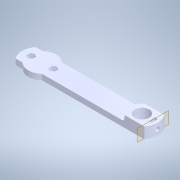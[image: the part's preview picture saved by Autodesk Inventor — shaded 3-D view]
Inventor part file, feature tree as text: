
AUTODESK INVENTOR PART (.ipt)
format: ipt  version: 2021 (Build 250183000, 183)  size: 411,648 bytes
history: native  units: in
note: dims shown in document units (in); Inventor stores cm internally (conversion verified against a paired STEP export)
features: sketch x20, extrude x17, fillet x3, projected_geometry x2, delete_face x1, chamfer x1, hole x1, plane x1, other x1
ambient origin geometry x8: Origin, YZ Plane, XZ Plane, XY Plane, X Axis, Y Axis, Z Axis, Center Point
bodies: Solid1 (feature_tree)
feature tree (47):
  extrude  "Extrusion1"  Depth=0.3937in TaperAngle=0.0deg
  extrude  "Extrusion2"  TaperAngle=0.0deg  [1 undecoded]
  sketch  "Sketch5"  dims[d9=0.3937in d10=0.0in d11=0.878in d12=0.3937in d13=0.0in]
  delete_face  "Delete Face1"
  extrude  "Extrusion4"  Depth=0.9843in
  extrude  "Extrusion5"  Depth=0.878in
  chamfer  "Chamfer1"  Distance=0.3937in
  sketch  "Sketch8"  dims[d32=0.3937in d33=0.0in d34=0.0787in d35=0.0787in d36=0.0in]
  extrude  "Extrusion7"  Depth=0.0787in
  extrude  "Extrusion9"  Depth=3.5433in
  extrude  "Extrusion8"  Depth=0.0787in
  fillet  "Fillet2"  Radius=0.0787in
  hole  "Hole1"  [1 undecoded]
  extrude  "Extrusion10"  Depth=0.0787in
  extrude  "Extrusion11"  Depth=0.0787in
  extrude  "Extrusion12"  Depth=0.1378in
  fillet  "Fillet3"  Radius=0.3937in
  extrude  "Extrusion3"  Depth=0.0118in
  extrude  "Extrusion13"  Depth=0.0394in
  extrude  "Extrusion14"  TaperAngle=0.0deg  [1 undecoded]
  extrude  "Extrusion15"  Depth=0.5906in
  extrude  "Extrusion16"  Depth=0.3937in TaperAngle=0.0deg
  plane  "Work Plane1"
  extrude  "Extrusion17"  Depth=0.3937in TaperAngle=0.0deg
  extrude  "Extrusion18"  Depth=0.3937in
  fillet  "Fillet4"  Radius=0.1969in
  sketch  "Sketch1"  dims[d0=0.7874in d1=0.3937in d2=0.0in]
  sketch  "Sketch2"  dims[d3=0.3937in d4=0.0in d5=0.0in]
  sketch  "Sketch4"  dims[d6=0.3937in d7=0.0in d8=0.9843in]
  sketch  "Sketch6"  dims[d14=0.0197in d15=0.0787in d16=45.0deg d28=0.7087in]
  sketch  "Sketch7"  dims[d29=0.3937in d30=0.0in d31=3.5433in]
  sketch  "Sketch11"  dims[d37=0.7874in d39=0.4921in]
  sketch  "Sketch12"  dims[d40=0.1378in d41=0.2362in d42=0.1575in d43=0.0787in d44=90.0deg d45=0.315in d46=0.8108in d47=0.2264in]
  sketch  "Sketch13"  dims[d48=0.0787in d49=0.0in d50=1.1811in]
  sketch  "Sketch14"  dims[d52=0.1181in d53=0.1378in d54=0.3937in d55=0.0in]
  projected_geometry  "Projected Loop3"
  projected_geometry  "Projected Loop4"
  sketch  "Sketch15"  dims[d56=0.0472in d57=0.0118in]
  sketch  "Sketch16"  dims[d60=0.0591in d61=0.0in d62=0.0394in]
  sketch  "Sketch17"  dims[d63=0.5118in d64=0.0in d65=0.0in]
  sketch  "Sketch18"  dims[d66=0.2362in d67=0.5906in]
  sketch  "Sketch19"  dims[d68=0.9843in d69=0.3937in d70=0.0in]
  sketch  "Sketch20"  dims[d71=1.1811in d72=0.3937in d73=0.0in]
  sketch  "Sketch21"  dims[d74=0.3937in d75=0.0in d76=0.3937in d77=0.1969in]
  sketch  "Sketch22"  dims[d78=0.1378in]
  sketch  "Sketch23"  dims[d79=0.5906in d80=0.0in d81=0.4331in d82=0.2283in d83=0.1063in d84=0.0in d85=0.0787in]
  other  "Cut-Extrude3"
note: 3 required parameter values undecoded (feature->parameter linkage not recoverable at this tier; creation-order binding heuristic only, values carry confidence <= 0.55)
